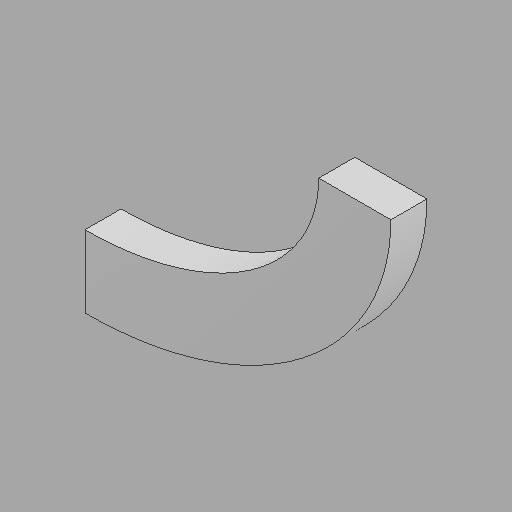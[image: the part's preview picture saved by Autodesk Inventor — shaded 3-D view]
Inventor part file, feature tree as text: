
AUTODESK INVENTOR PART (.ipt)
format: ipt  version: 2022.1 (Build 261234020, 234B)  size: 92,672 bytes
history: imported  units: in
note: dims shown in document units (in); Inventor stores cm internally (conversion verified against a paired STEP export)
features: imported_body x1
ambient origin geometry x8: Origin, YZ Plane, XZ Plane, XY Plane, X Axis, Y Axis, Z Axis, Center Point
bodies: Solid1 (imported_parasolid), Body1 (imported_parasolid)
feature tree (1):
  imported_body  NMx_Import_Brep_tag  [imported B-rep: ~6 faces, bbox_mm=[1292.218346, 987.422025, 152.4]]
